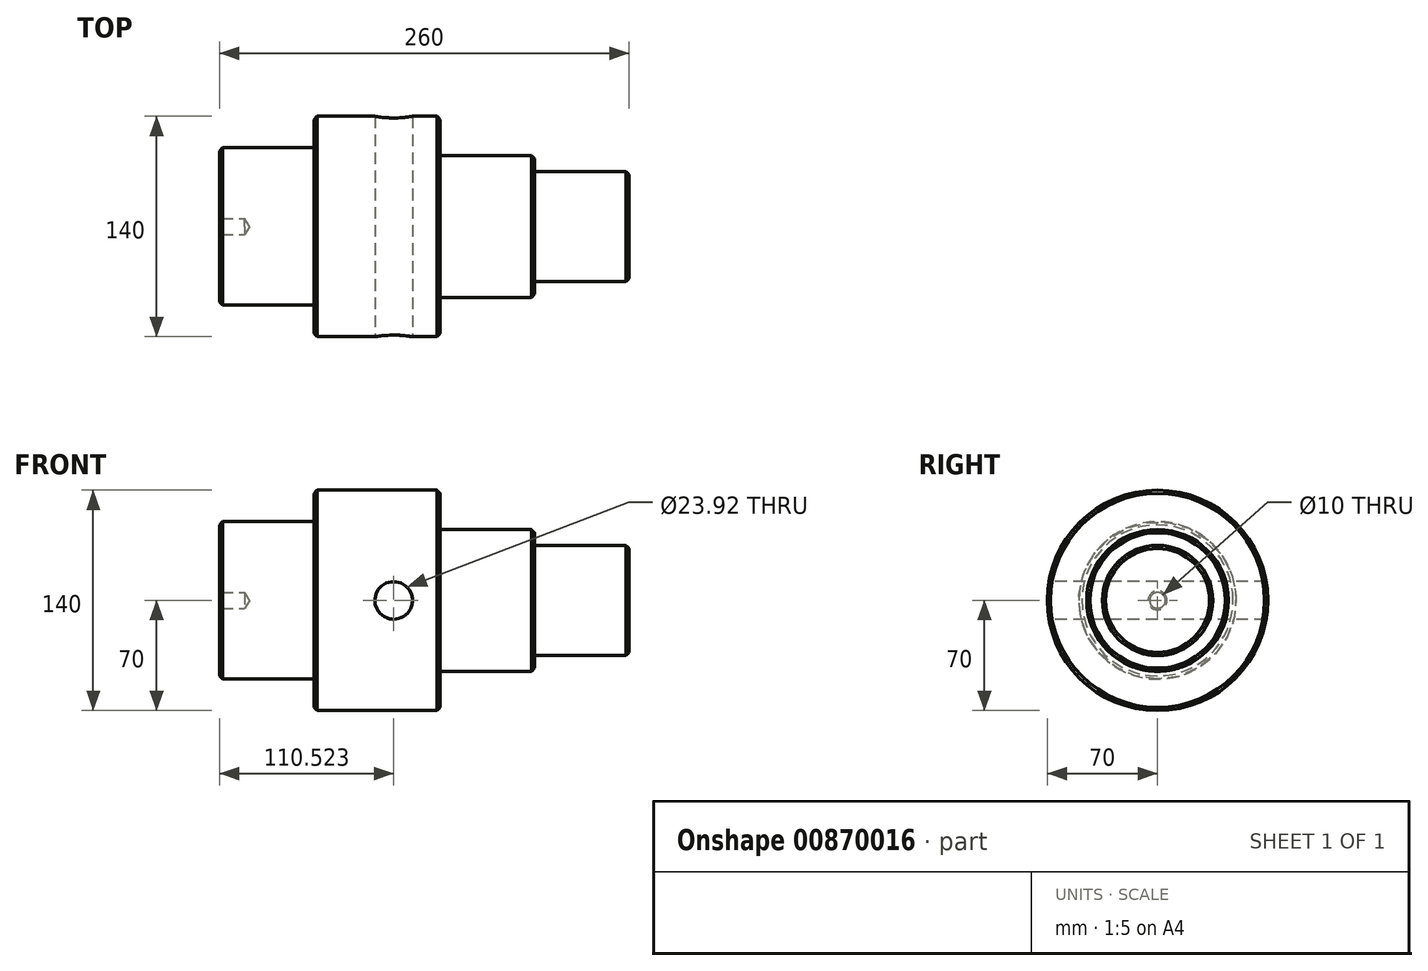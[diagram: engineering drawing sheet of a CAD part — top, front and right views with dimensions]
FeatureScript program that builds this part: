
annotation { "Feature Type Name" : "Feature", "Feature Type Description" : "" }
export const myFeature = defineFeature(function(context is Context, id is Id, definition is map)
    precondition{}
    {
        {
            var Q0;
            Q0=qCreatedBy(makeId("Front.planeOp"),FACE);
            var sketch = newSketch(context, id + "F0", { "sketchPlane" : qUnion([Q0])});
            skLineSegment(sketch, "E0", {"start": v(0, 50) * mm, "end": v(60, 50) * mm});
            skLineSegment(sketch, "E1", {"start": v(60, 50) * mm, "end": v(60, 70) * mm});
            skLineSegment(sketch, "E2", {"start": v(60, 70) * mm, "end": v(140, 70) * mm});
            skLineSegment(sketch, "E3", {"start": v(140, 70) * mm, "end": v(140, 45) * mm});
            skLineSegment(sketch, "E4", {"start": v(140, 45) * mm, "end": v(200, 45) * mm});
            skLineSegment(sketch, "E5", {"start": v(200, 45) * mm, "end": v(200, 35) * mm});
            skLineSegment(sketch, "E6", {"start": v(260, 35) * mm, "end": v(260, 0) * mm});
            skLineSegment(sketch, "E7", {"start": v(260, 0) * mm, "end": v(0, 0) * mm});
            skLineSegment(sketch, "E8", {"start": v(0, 0) * mm, "end": v(0, 50) * mm});
            skLineSegment(sketch, "E9", {"start": v(200, 35) * mm, "end": v(260, 35) * mm});
            skSolve(sketch);
        }
        {
            var Q0;
            Q0=makeQuery(id+"F0.imprint","IMPRINT",FACE,{"disambiguationData":[TD([[makeQuery(id+"F0.imprint","IMPRINT",EDGE,{"derivedFrom":sQuery(id+"F0.wireOp",EDGE,"E0")}),-1.0]])]});
            var Q1;
            Q1=sQuery(id+"F0.wireOp",EDGE,"E7");
            revolve(context, id + "F1", {"surfaceOperationType" : NewSurfaceOperationType.NEW, "entities" : qUnion([Q0]), "axis" : qUnion([Q1]), "revolveType" : RevolveType.FULL});
        }
        {
            var Q0;
            Q0=makeQuery(id+"F1.opRevolve","SWEPT_EDGE",EDGE,{"disambiguationData":[OSD([sQuery(id+"F0.wireOp",EDGE,"E0"),sQuery(id+"F0.wireOp",EDGE,"E8")])]});
            var Q1;
            Q1=makeQuery(id+"F1.opRevolve","SWEPT_EDGE",EDGE,{"disambiguationData":[OSD([sQuery(id+"F0.wireOp",EDGE,"E1"),sQuery(id+"F0.wireOp",EDGE,"E2")])]});
            var Q2;
            Q2=makeQuery(id+"F1.opRevolve","SWEPT_EDGE",EDGE,{"disambiguationData":[OSD([sQuery(id+"F0.wireOp",EDGE,"E2"),sQuery(id+"F0.wireOp",EDGE,"E3")])]});
            var Q3;
            Q3=makeQuery(id+"F1.opRevolve","SWEPT_EDGE",EDGE,{"disambiguationData":[OSD([sQuery(id+"F0.wireOp",EDGE,"E4"),sQuery(id+"F0.wireOp",EDGE,"E5")])]});
            var Q4;
            Q4=makeQuery(id+"F1.opRevolve","SWEPT_EDGE",EDGE,{"disambiguationData":[OSD([sQuery(id+"F0.wireOp",EDGE,"E6"),sQuery(id+"F0.wireOp",EDGE,"E9")])]});
            chamfer(context, id + "F2", {"entities" : qUnion([Q0, Q1, Q2, Q3, Q4]), "width" : 2 * mm, "tangentPropagation" : true});
        }
        {
            var Q0;
            Q0=makeQuery(id+"F1.opRevolve","SWEPT_EDGE",EDGE,{"disambiguationData":[OSD([sQuery(id+"F0.wireOp",EDGE,"E0"),sQuery(id+"F0.wireOp",EDGE,"E1")])]});
            var Q1;
            Q1=makeQuery(id+"F1.opRevolve","SWEPT_EDGE",EDGE,{"disambiguationData":[OSD([sQuery(id+"F0.wireOp",EDGE,"E3"),sQuery(id+"F0.wireOp",EDGE,"E4")])]});
            var Q2;
            Q2=makeQuery(id+"F1.opRevolve","SWEPT_EDGE",EDGE,{"disambiguationData":[OSD([sQuery(id+"F0.wireOp",EDGE,"E5"),sQuery(id+"F0.wireOp",EDGE,"E9")])]});
            fillet(context, id + "F3", {"entities" : qUnion([Q0, Q1, Q2]), "radius" : 1 * mm, "tangentPropagation" : true, "rho" : 0.5, "crossSection" : FilletCrossSection.CONIC, "allowEdgeOverflow" : false});
        }
        {
            var Q0;
            Q0=makeQuery(id+"F1.opRevolve","SWEPT_FACE",FACE,{"disambiguationData":[OSD([sQuery(id+"F0.wireOp",EDGE,"E8")])]});
            var sketch = newSketch(context, id + "F4", { "sketchPlane" : qUnion([Q0])});
            skPoint(sketch, "E10", {"position": v(0, 0) * mm});
            skSolve(sketch);
        }
        {
            var Q0;
            Q0=sQuery(id+"F4.wireOp",VERTEX,"E10");
            var Q1;
            Q1=makeQuery(id+"F1.opRevolve","SWEPT_BODY",BODY,{"disambiguationData":[OSD([sQuery(id+"F0.wireOp",EDGE,"E0"),sQuery(id+"F0.wireOp",EDGE,"E1"),sQuery(id+"F0.wireOp",EDGE,"E2"),sQuery(id+"F0.wireOp",EDGE,"E3"),sQuery(id+"F0.wireOp",EDGE,"E4"),sQuery(id+"F0.wireOp",EDGE,"E5"),sQuery(id+"F0.wireOp",EDGE,"E6"),sQuery(id+"F0.wireOp",EDGE,"E7"),sQuery(id+"F0.wireOp",EDGE,"E8"),sQuery(id+"F0.wireOp",EDGE,"E9")])]});
            hole(context, id + "F5", {"style" : HoleStyle.C_SINK, "endStyle" : HoleEndStyle.BLIND, "holeDiameter" : 10 * mm, "cSinkDiameter" : 12 * mm, "cSinkAngle" : 90 * degree, "majorDiameter" : 5 * mm, "holeDepth" : 16 * mm, "isTappedThrough" : true, "tappedDepth" : 12 * mm, "tapClearance" : 3, "locations" : qUnion([Q0]), "scope" : qUnion([Q1]), "startStyle" : HoleStartStyle.SKETCH});
        }
        {
            var Q0;
            Q0=qCreatedBy(makeId("Front.planeOp"),FACE);
            var sketch = newSketch(context, id + "F6", { "sketchPlane" : qUnion([Q0])});
            skCircle(sketch, "E11", {"center": v(110.52, 0) * mm, "radius": 11.96 * mm});
            skLineSegment(sketch, "E12", {"start": v(62, 70) * mm, "end": v(138, 70) * mm});
            skLineSegment(sketch, "E13", {"start": v(62, 70) * mm, "end": v(138, 70) * mm, "construction": true});
            skSolve(sketch);
        }
        {
            var Q0;
            Q0 = qSketchRegion(id + "F6", true);
            extrude(context, id + "F7", {"entities" : qUnion([Q0]), "operationType" : NewBodyOperationType.REMOVE, "endBound" : BoundingType.THROUGH_ALL, "oppositeDirection" : true, "depth" : 25 * mm, "offsetDistance" : 25 * mm, "hasSecondDirection" : true, "secondDirectionBound" : BoundingType.THROUGH_ALL, "secondDirectionOppositeDirection" : false, "secondDirectionDepth" : 25 * mm});
        }
    });
